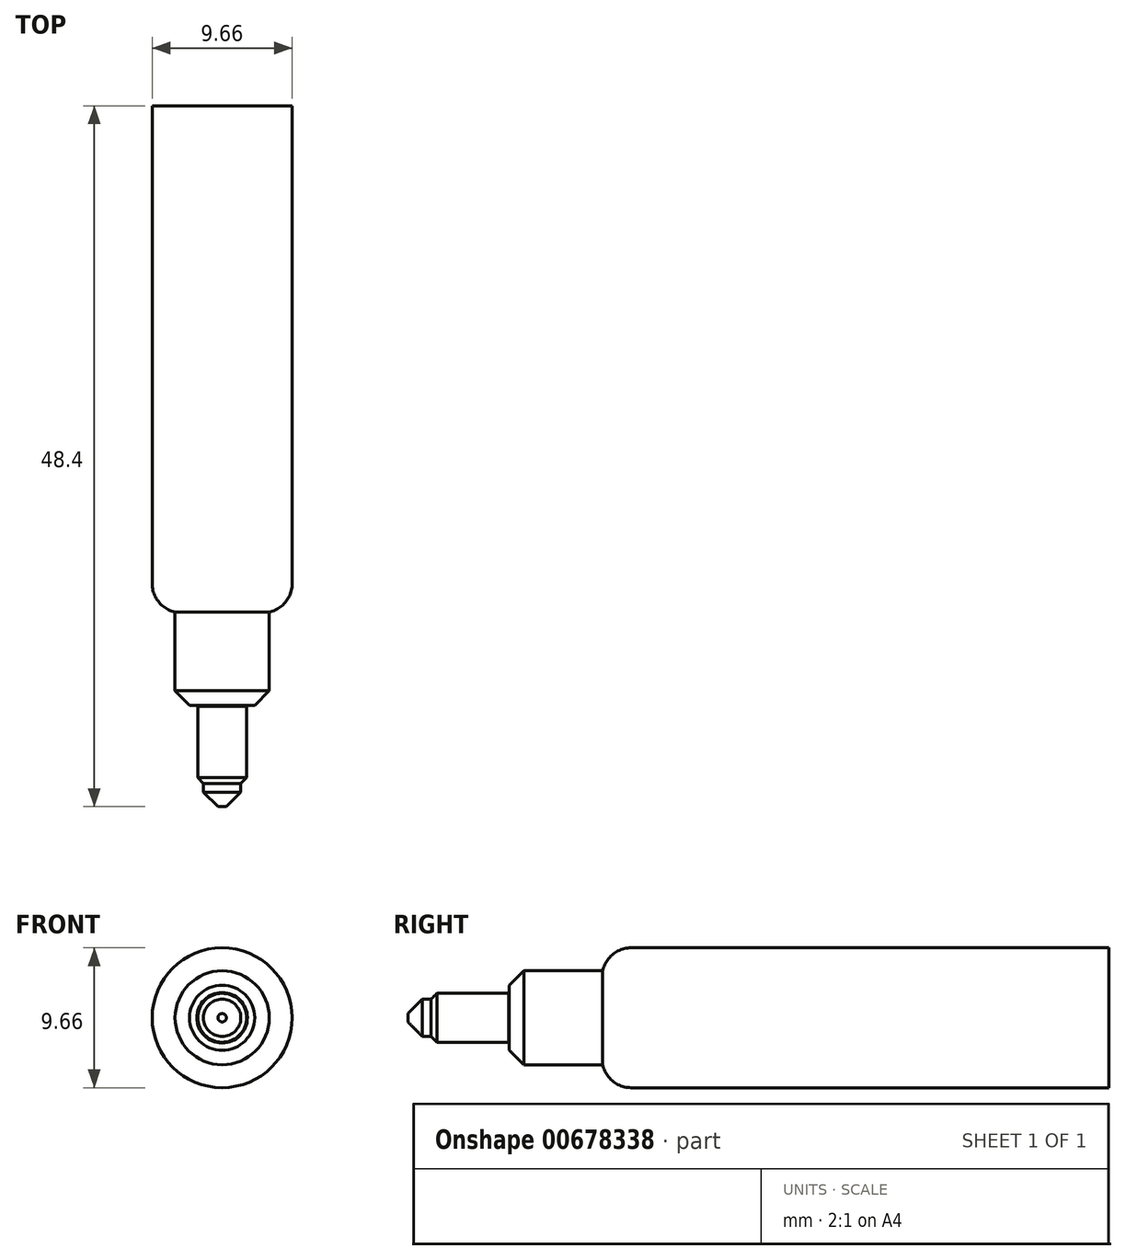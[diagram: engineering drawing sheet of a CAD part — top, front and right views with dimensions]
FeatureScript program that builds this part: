
annotation { "Feature Type Name" : "Feature", "Feature Type Description" : "" }
export const myFeature = defineFeature(function(context is Context, id is Id, definition is map)
    precondition{}
    {
        {
            var Q0;
            Q0=qCreatedBy(makeId("Front.planeOp"),FACE);
            var sketch = newSketch(context, id + "F0", { "sketchPlane" : qUnion([Q0])});
            skCircle(sketch, "E0", {"center": v(0, 0) * mm, "radius": 4.83 * mm});
            skSolve(sketch);
        }
        {
            var Q0;
            Q0 = qSketchRegion(id + "F0", true);
            extrude(context, id + "F1", {"entities" : qUnion([Q0]), "depth" : 25 * mm, "offsetDistance" : 25 * mm});
        }
        {
            var Q0;
            Q0=makeQuery(id+"F1.opExtrude","CAP_FACE",FACE,{"disambiguationData":[OSD([sQuery(id+"F0.wireOp",EDGE,"E0")])],"isStart":false});
            extrude(context, id + "F2", {"entities" : qUnion([Q0]), "operationType" : NewBodyOperationType.ADD, "depth" : 10 * mm, "offsetDistance" : 25 * mm});
        }
        {
            var Q0;
            Q0=makeQuery(id+"F2.opExtrude","CAP_EDGE",EDGE,{"disambiguationData":[OSD([sQuery(id+"F0.wireOp",EDGE,"E0")])],"isStart":false});
            fillet(context, id + "F3", {"entities" : qUnion([Q0]), "radius" : 2 * mm, "tangentPropagation" : true, "allowEdgeOverflow" : false});
        }
        {
            var Q0;
            Q0=qCreatedBy(makeId("Front.planeOp"),FACE);
            var sketch = newSketch(context, id + "F4", { "sketchPlane" : qUnion([Q0])});
            skCircle(sketch, "E1", {"center": v(0, 0) * mm, "radius": 1.59 * mm});
            skSolve(sketch);
        }
        {
            var Q0;
            Q0 = qSketchRegion(id + "F4", true);
            extrude(context, id + "F5", {"entities" : qUnion([Q0]), "operationType" : NewBodyOperationType.REMOVE, "depth" : 0.5 * mm, "offsetDistance" : 25 * mm});
        }
        {
            var Q0;
            Q0=qCreatedBy(makeId("Front.planeOp"),FACE);
            var sketch = newSketch(context, id + "F6", { "sketchPlane" : qUnion([Q0])});
            skCircle(sketch, "E2", {"center": v(0, 0) * mm, "radius": 2.65 * mm});
            skSolve(sketch);
        }
        {
            var Q0;
            Q0 = qSketchRegion(id + "F6", true);
            extrude(context, id + "F7", {"entities" : qUnion([Q0]), "operationType" : NewBodyOperationType.ADD, "depth" : 41.5 * mm, "offsetDistance" : 25 * mm});
        }
        {
            var Q0;
            Q0=qCreatedBy(makeId("Front.planeOp"),FACE);
            var sketch = newSketch(context, id + "F8", { "sketchPlane" : qUnion([Q0])});
            skCircle(sketch, "E3", {"center": v(0, 0) * mm, "radius": 1.69 * mm});
            skSolve(sketch);
        }
        {
            var Q0;
            Q0 = qSketchRegion(id + "F8", true);
            extrude(context, id + "F9", {"entities" : qUnion([Q0]), "operationType" : NewBodyOperationType.ADD, "depth" : 47.4 * mm, "offsetDistance" : 25 * mm});
        }
        {
            var Q0;
            Q0=makeQuery(id+"F9.opExtrude","CAP_EDGE",EDGE,{"disambiguationData":[OSD([sQuery(id+"F8.wireOp",EDGE,"E3")])],"isStart":false});
            var Q1;
            Q1=makeQuery(id+"F7.opExtrude","CAP_EDGE",EDGE,{"disambiguationData":[OSD([sQuery(id+"F6.wireOp",EDGE,"E2")])],"isStart":false});
            chamfer(context, id + "F10", {"entities" : qUnion([Q0, Q1]), "width" : 1 * mm, "tangentPropagation" : true});
        }
        {
            var Q0;
            Q0=qCreatedBy(makeId("Front.planeOp"),FACE);
            var sketch = newSketch(context, id + "F11", { "sketchPlane" : qUnion([Q0])});
            skCircle(sketch, "E4", {"center": v(0, 0) * mm, "radius": 3.25 * mm});
            skSolve(sketch);
        }
        {
            var Q0;
            Q0 = qSketchRegion(id + "F11", true);
            extrude(context, id + "F12", {"entities" : qUnion([Q0]), "operationType" : NewBodyOperationType.ADD, "depth" : 41.4 * mm, "offsetDistance" : 25 * mm});
        }
        {
            var Q0;
            Q0=makeQuery(id+"F12.opExtrude","CAP_EDGE",EDGE,{"disambiguationData":[OSD([sQuery(id+"F11.wireOp",EDGE,"E4")])],"isStart":false});
            chamfer(context, id + "F13", {"entities" : qUnion([Q0]), "width" : 1 * mm, "tangentPropagation" : true});
        }
        {
            var Q0;
            Q0=qCreatedBy(makeId("Front.planeOp"),FACE);
            var sketch = newSketch(context, id + "F14", { "sketchPlane" : qUnion([Q0])});
            skCircle(sketch, "E5", {"center": v(0, 0) * mm, "radius": 1.29 * mm});
            skSolve(sketch);
        }
        {
            var Q0;
            Q0 = qSketchRegion(id + "F14", true);
            extrude(context, id + "F15", {"entities" : qUnion([Q0]), "operationType" : NewBodyOperationType.ADD, "depth" : 48.4 * mm, "offsetDistance" : 25 * mm});
        }
        {
            var Q0;
            Q0=makeQuery(id+"F15.opExtrude","CAP_EDGE",EDGE,{"disambiguationData":[OSD([sQuery(id+"F14.wireOp",EDGE,"E5")])],"isStart":false});
            chamfer(context, id + "F16", {"entities" : qUnion([Q0]), "width" : 1 * mm, "tangentPropagation" : true});
        }
    });
